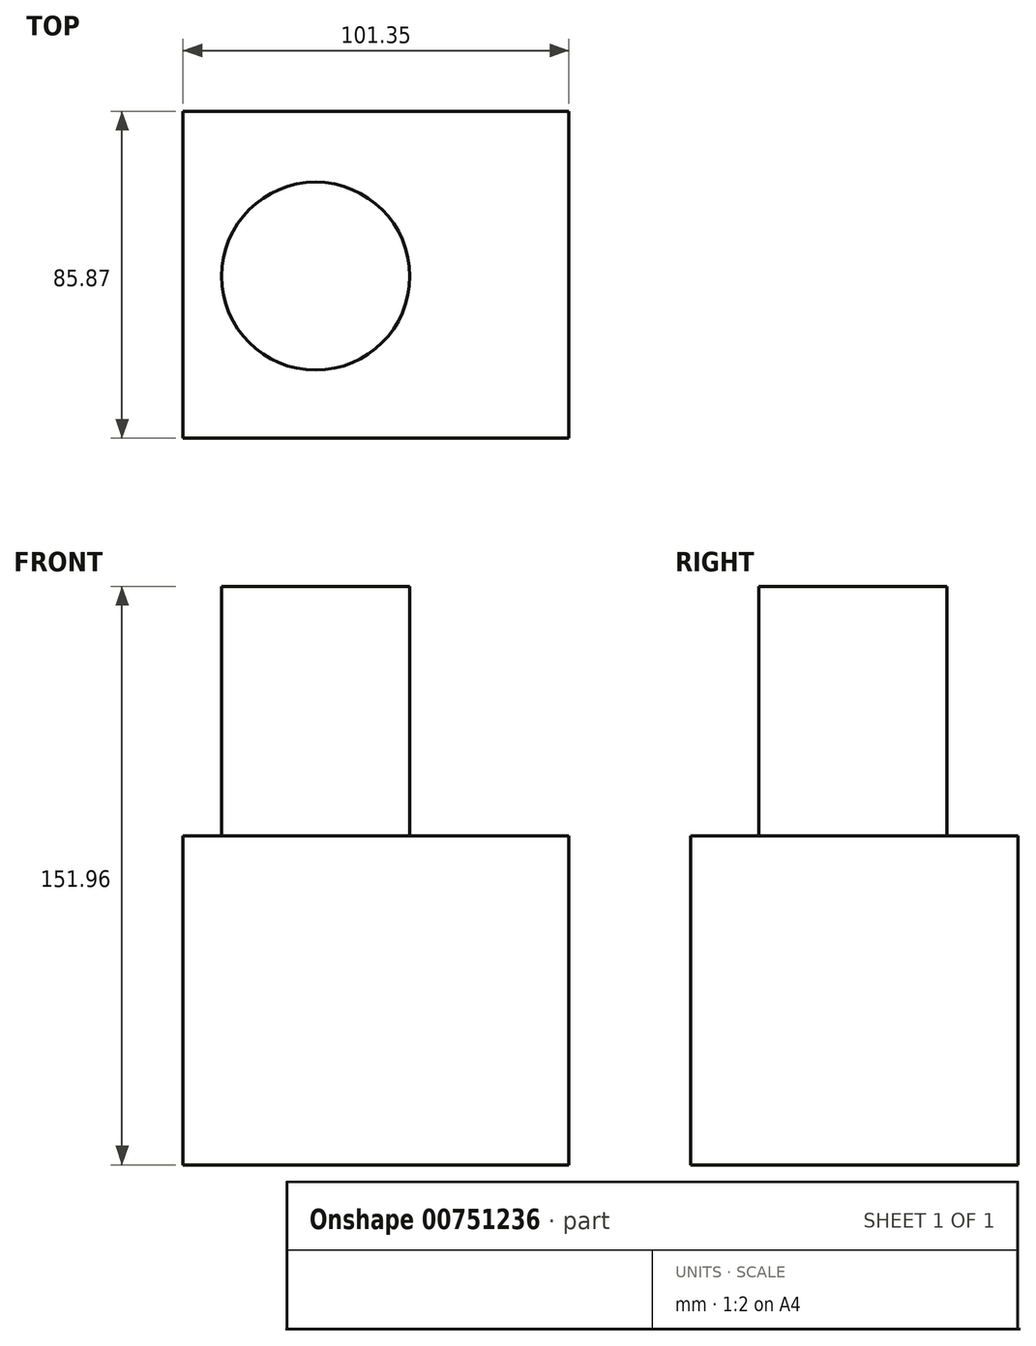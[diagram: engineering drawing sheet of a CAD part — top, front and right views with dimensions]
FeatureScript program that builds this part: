
annotation { "Feature Type Name" : "Feature", "Feature Type Description" : "" }
export const myFeature = defineFeature(function(context is Context, id is Id, definition is map)
    precondition{}
    {
        {
            var Q0;
            Q0=qCreatedBy(makeId("Right.planeOp"),FACE);
            var sketch = newSketch(context, id + "F0", { "sketchPlane" : qUnion([Q0])});
            skLineSegment(sketch, "E0.bottom", {"start": v(-30.58, 47.2) * mm, "end": v(55.29, 47.2) * mm});
            skLineSegment(sketch, "E0.top", {"start": v(-30.58, -39.22) * mm, "end": v(55.29, -39.22) * mm});
            skLineSegment(sketch, "E0.left", {"start": v(-30.58, 47.2) * mm, "end": v(-30.58, -39.22) * mm});
            skLineSegment(sketch, "E0.right", {"start": v(55.29, 47.2) * mm, "end": v(55.29, -39.22) * mm});
            skSolve(sketch);
        }
        {
            var Q0;
            Q0=makeQuery(id+"F0.imprint","IMPRINT",FACE,{"disambiguationData":[TD([[makeQuery(id+"F0.imprint","IMPRINT",EDGE,{"derivedFrom":sQuery(id+"F0.wireOp",EDGE,"E0.bottom")}),-1.0]])]});
            extrude(context, id + "F1", {"entities" : qUnion([Q0]), "depth" : 101.35 * mm, "offsetDistance" : 25.4 * mm});
        }
        {
            var Q0;
            Q0=makeQuery(id+"F1.opExtrude","SWEPT_FACE",FACE,{"disambiguationData":[OSD([sQuery(id+"F0.wireOp",EDGE,"E0.bottom")])]});
            var sketch = newSketch(context, id + "F2", { "sketchPlane" : qUnion([Q0])});
            skCircle(sketch, "E1", {"center": v(34.83, 11.98) * mm, "radius": 24.7 * mm});
            skSolve(sketch);
        }
        {
            var Q0;
            Q0=makeQuery(id+"F2.imprint","IMPRINT",FACE,{"disambiguationData":[TD([[makeQuery(id+"F2.imprint","IMPRINT",EDGE,{"derivedFrom":sQuery(id+"F2.wireOp",EDGE,"E1")}),1.0]])]});
            extrude(context, id + "F3", {"entities" : qUnion([Q0]), "operationType" : NewBodyOperationType.ADD, "depth" : 65.53 * mm, "offsetDistance" : 25.4 * mm});
        }
    });
